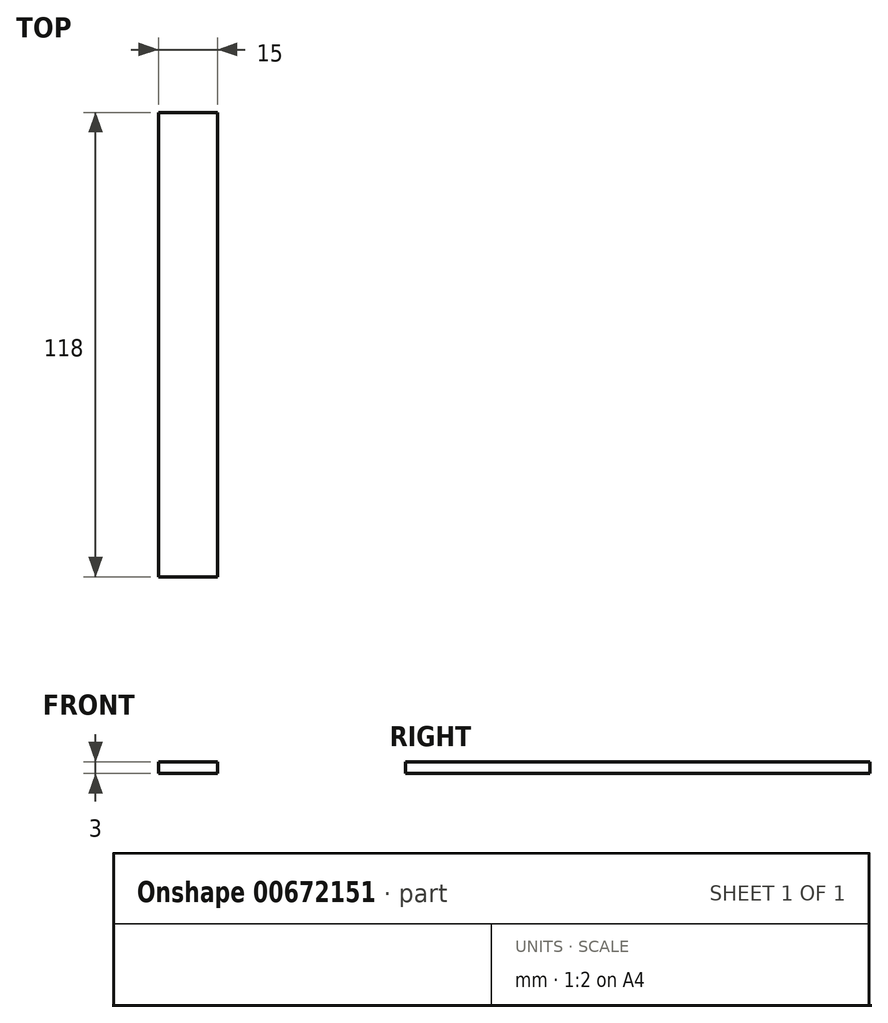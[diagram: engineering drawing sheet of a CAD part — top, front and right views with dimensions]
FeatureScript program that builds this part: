
annotation { "Feature Type Name" : "Feature", "Feature Type Description" : "" }
export const myFeature = defineFeature(function(context is Context, id is Id, definition is map)
    precondition{}
    {
        {
            var Q0;
            Q0=qCreatedBy(makeId("Top.planeOp"),FACE);
            var sketch = newSketch(context, id + "F0", { "sketchPlane" : qUnion([Q0])});
            skLineSegment(sketch, "E0.bottom", {"start": v(-14.7, 67.58) * mm, "end": v(0.3, 67.58) * mm});
            skLineSegment(sketch, "E0.top", {"start": v(-14.7, -50.42) * mm, "end": v(0.3, -50.42) * mm});
            skLineSegment(sketch, "E0.left", {"start": v(-14.7, 67.58) * mm, "end": v(-14.7, -50.42) * mm});
            skLineSegment(sketch, "E0.right", {"start": v(0.3, 67.58) * mm, "end": v(0.3, -50.42) * mm});
            skLineSegment(sketch, "E1", {"start": v(-7.2, 67.58) * mm, "end": v(-7.2, -50.42) * mm, "construction": true});
            skSolve(sketch);
        }
        {
            var Q0;
            Q0 = qSketchRegion(id + "F0", true);
            extrude(context, id + "F1", {"entities" : qUnion([Q0]), "depth" : 3 * mm, "offsetDistance" : 25 * mm});
        }
    });
